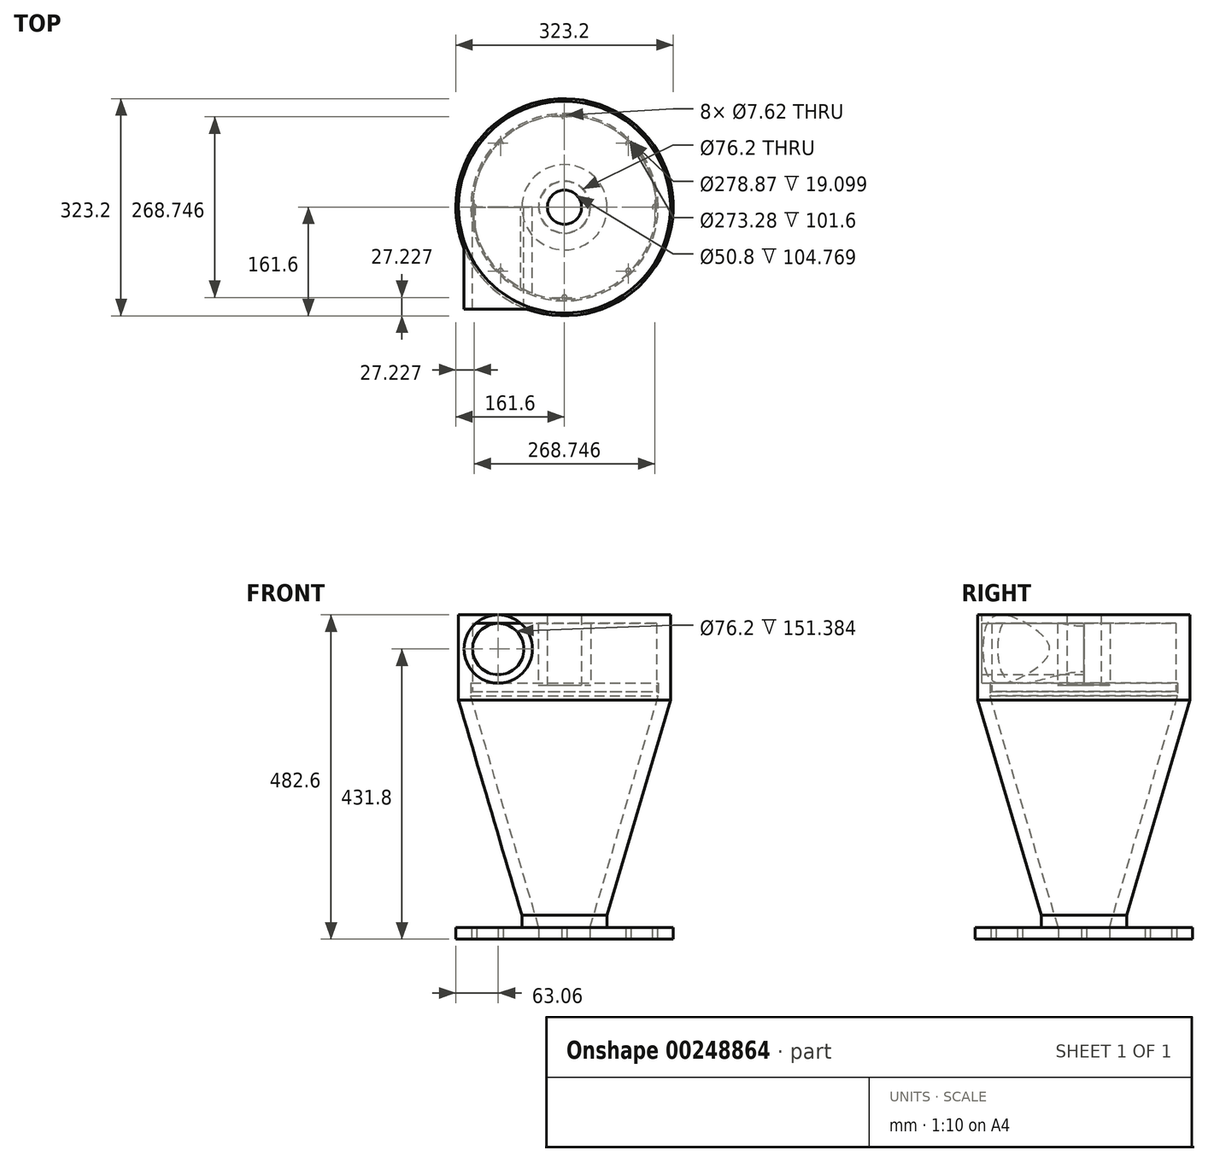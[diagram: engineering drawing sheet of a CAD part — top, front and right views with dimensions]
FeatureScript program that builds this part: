
annotation { "Feature Type Name" : "Feature", "Feature Type Description" : "" }
export const myFeature = defineFeature(function(context is Context, id is Id, definition is map)
    precondition{}
    {
        {
            var Q0;
            Q0=qCreatedBy(makeId("Front.planeOp"),FACE);
            var sketch = newSketch(context, id + "F0", { "sketchPlane" : qUnion([Q0])});
            skLineSegment(sketch, "E0.bottom", {"start": v(-38.1, 0) * mm, "end": v(-161.6, 0) * mm});
            skLineSegment(sketch, "E0.top", {"start": v(-63.5, 17.43) * mm, "end": v(-161.6, 17.43) * mm});
            skLineSegment(sketch, "E0.left", {"start": v(-38.1, 0) * mm, "end": v(-38.1, 17.43) * mm});
            skLineSegment(sketch, "E0.right", {"start": v(-161.6, 0) * mm, "end": v(-161.6, 17.43) * mm});
            skLineSegment(sketch, "E1", {"start": v(-38.1, 17.43) * mm, "end": v(-139.43, 361.9) * mm});
            skLineSegment(sketch, "E2", {"start": v(-157.57, 355.6) * mm, "end": v(-63.5, 35.82) * mm});
            skLineSegment(sketch, "E3", {"start": v(-63.5, 17.43) * mm, "end": v(-63.5, 35.82) * mm});
            skLineSegment(sketch, "E4", {"start": v(0, -75.28) * mm, "end": v(0, 555.19) * mm, "construction": true});
            skLineSegment(sketch, "E5.right", {"start": v(-139.43, 361.9) * mm, "end": v(-139.43, 361.9) * mm});
            skLineSegment(sketch, "E6.top", {"start": v(-139.43, 381) * mm, "end": v(-157.57, 381) * mm});
            skLineSegment(sketch, "E6.left", {"start": v(-139.43, 361.9) * mm, "end": v(-139.43, 381) * mm});
            skLineSegment(sketch, "E6.right", {"start": v(-157.57, 355.6) * mm, "end": v(-157.57, 381) * mm});
            skSolve(sketch);
        }
        {
            var Q0;
            Q0 = qSketchRegion(id + "F0", true);
            var Q1;
            Q1=sQuery(id+"F0.wireOp",EDGE,"E4");
            revolve(context, id + "F1", {"entities" : qUnion([Q0]), "axis" : qUnion([Q1]), "revolveType" : RevolveType.FULL});
        }
        {
            var Q0;
            Q0=makeQuery(id+"F1.opRevolve","SWEPT_FACE",FACE,{"disambiguationData":[OSD([sQuery(id+"F0.wireOp",EDGE,"E0.bottom")])]});
            var sketch = newSketch(context, id + "F2", { "sketchPlane" : qUnion([Q0])});
            skCircle(sketch, "E7", {"center": v(0, 134.37) * mm, "radius": 3.81 * mm});
            skLineSegment(sketch, "E8", {"start": v(0, 38.1) * mm, "end": v(0, 161.6) * mm, "construction": true});
            skCircle(sketch, "E9", {"center": v(0, 0) * mm, "radius": 134.37 * mm, "construction": true});
            skCircle(sketch, "E10.1.0", {"center": v(-95.02, 95.02) * mm, "radius": 3.81 * mm});
            skCircle(sketch, "E10.2.0", {"center": v(-134.37, 0) * mm, "radius": 3.81 * mm});
            skCircle(sketch, "E10.3.0", {"center": v(-95.02, -95.02) * mm, "radius": 3.81 * mm});
            skCircle(sketch, "E10.4.0", {"center": v(0, -134.37) * mm, "radius": 3.81 * mm});
            skCircle(sketch, "E10.5.0", {"center": v(95.02, -95.02) * mm, "radius": 3.81 * mm});
            skCircle(sketch, "E10.6.0", {"center": v(134.37, 0) * mm, "radius": 3.81 * mm});
            skCircle(sketch, "E10.7.0", {"center": v(95.02, 95.02) * mm, "radius": 3.81 * mm});
            skSolve(sketch);
        }
        {
            var Q0;
            Q0=makeQuery(id+"F2.imprint","IMPRINT",FACE,{"disambiguationData":[TD([[makeQuery(id+"F2.imprint","IMPRINT",EDGE,{"derivedFrom":sQuery(id+"F2.wireOp",EDGE,"E10.5.0")}),1.0]])]});
            var Q1;
            Q1=makeQuery(id+"F2.imprint","IMPRINT",FACE,{"disambiguationData":[TD([[makeQuery(id+"F2.imprint","IMPRINT",EDGE,{"derivedFrom":sQuery(id+"F2.wireOp",EDGE,"E10.4.0")}),1.0]])]});
            var Q2;
            Q2=makeQuery(id+"F2.imprint","IMPRINT",FACE,{"disambiguationData":[TD([[makeQuery(id+"F2.imprint","IMPRINT",EDGE,{"derivedFrom":sQuery(id+"F2.wireOp",EDGE,"E10.3.0")}),1.0]])]});
            var Q3;
            Q3=makeQuery(id+"F2.imprint","IMPRINT",FACE,{"disambiguationData":[TD([[makeQuery(id+"F2.imprint","IMPRINT",EDGE,{"derivedFrom":sQuery(id+"F2.wireOp",EDGE,"E10.2.0")}),1.0]])]});
            var Q4;
            Q4=makeQuery(id+"F2.imprint","IMPRINT",FACE,{"disambiguationData":[TD([[makeQuery(id+"F2.imprint","IMPRINT",EDGE,{"derivedFrom":sQuery(id+"F2.wireOp",EDGE,"E10.1.0")}),1.0]])]});
            var Q5;
            Q5=makeQuery(id+"F2.imprint","IMPRINT",FACE,{"disambiguationData":[TD([[makeQuery(id+"F2.imprint","IMPRINT",EDGE,{"derivedFrom":sQuery(id+"F2.wireOp",EDGE,"E7")}),1.0]])]});
            var Q6;
            Q6=makeQuery(id+"F2.imprint","IMPRINT",FACE,{"disambiguationData":[TD([[makeQuery(id+"F2.imprint","IMPRINT",EDGE,{"derivedFrom":sQuery(id+"F2.wireOp",EDGE,"E10.6.0")}),1.0]])]});
            var Q7;
            Q7=makeQuery(id+"F2.imprint","IMPRINT",FACE,{"disambiguationData":[TD([[makeQuery(id+"F2.imprint","IMPRINT",EDGE,{"derivedFrom":sQuery(id+"F2.wireOp",EDGE,"E10.7.0")}),1.0]])]});
            var Q8;
            Q8=sQuery(id+"F2.wireOp",EDGE,"E10.1.0");
            var Q9;
            Q9=sQuery(id+"F2.wireOp",EDGE,"E7");
            var Q10;
            Q10=sQuery(id+"F2.wireOp",EDGE,"E10.7.0");
            var Q11;
            Q11=sQuery(id+"F2.wireOp",EDGE,"E10.6.0");
            var Q12;
            Q12=sQuery(id+"F2.wireOp",EDGE,"E10.5.0");
            var Q13;
            Q13=sQuery(id+"F2.wireOp",EDGE,"E10.4.0");
            var Q14;
            Q14=sQuery(id+"F2.wireOp",EDGE,"E10.3.0");
            var Q15;
            Q15=sQuery(id+"F2.wireOp",EDGE,"E10.2.0");
            extrude(context, id + "F3", {"entities" : qUnion([Q0, Q1, Q2, Q3, Q4, Q5, Q6, Q7]), "operationType" : NewBodyOperationType.REMOVE, "surfaceEntities" : qUnion([Q8, Q9, Q10, Q11, Q12, Q13, Q14, Q15]), "endBound" : BoundingType.UP_TO_NEXT, "oppositeDirection" : true, "depth" : 25.4 * mm});
        }
        {
            var Q0;
            Q0=qCreatedBy(makeId("Front.planeOp"),FACE);
            var sketch = newSketch(context, id + "F4", { "sketchPlane" : qUnion([Q0])});
            skLineSegment(sketch, "E11", {"start": v(-139.18, 368.3) * mm, "end": v(-139.43, 368.3) * mm, "construction": true});
            skLineSegment(sketch, "E12.bottom", {"start": v(-139.18, 368.3) * mm, "end": v(-136.64, 368.3) * mm});
            skLineSegment(sketch, "E12.left", {"start": v(-139.18, 368.3) * mm, "end": v(-139.18, 381) * mm});
            skLineSegment(sketch, "E12.right", {"start": v(-136.64, 368.3) * mm, "end": v(-136.64, 469.9) * mm});
            skLineSegment(sketch, "E13.top", {"start": v(-139.18, 381) * mm, "end": v(-157.57, 381) * mm});
            skLineSegment(sketch, "E13.right", {"start": v(-157.57, 469.9) * mm, "end": v(-157.57, 381) * mm});
            skLineSegment(sketch, "E14.bottom", {"start": v(-136.64, 469.9) * mm, "end": v(-38.8, 469.9) * mm});
            skLineSegment(sketch, "E14.top", {"start": v(-157.57, 482.6) * mm, "end": v(-25.4, 482.6) * mm});
            skLineSegment(sketch, "E14.left", {"start": v(-157.57, 469.9) * mm, "end": v(-157.57, 482.6) * mm});
            skLineSegment(sketch, "E15.bottom", {"start": v(-25.4, 482.6) * mm, "end": v(-38.8, 482.6) * mm});
            skLineSegment(sketch, "E15.top", {"start": v(-25.4, 377.83) * mm, "end": v(-38.8, 377.83) * mm});
            skLineSegment(sketch, "E15.left", {"start": v(-25.4, 482.6) * mm, "end": v(-25.4, 377.83) * mm});
            skLineSegment(sketch, "E15.right", {"start": v(-38.8, 469.9) * mm, "end": v(-38.8, 377.83) * mm});
            skPoint(sketch, "E14.right.end.orphan", {"position": v(0, 482.6) * mm});
            skCircle(sketch, "E16", {"center": v(-98.54, 431.8) * mm, "radius": 38.1 * mm, "construction": true});
            skPoint(sketch, "E16.first.point", {"position": v(-136.64, 431.8) * mm});
            skPoint(sketch, "E16.second.point", {"position": v(-87.72, 468.33) * mm});
            skPoint(sketch, "E16.second.point.positionSnap0", {"position": v(-87.72, 469.9) * mm});
            skPoint(sketch, "E16.third.point", {"position": v(-60.47, 430.37) * mm});
            skSolve(sketch);
        }
        {
            var Q0;
            Q0 = qSketchRegion(id + "F4", true);
            var Q1;
            Q1=sQuery(id+"F0.wireOp",EDGE,"E4");
            revolve(context, id + "F5", {"entities" : qUnion([Q0]), "axis" : qUnion([Q1]), "revolveType" : RevolveType.FULL});
        }
        {
            var Q0;
            Q0=qCreatedBy(makeId("Front.planeOp"),FACE);
            var sketch = newSketch(context, id + "F6", { "sketchPlane" : qUnion([Q0])});
            skCircle(sketch, "E17", {"center": v(-98.54, 431.8) * mm, "radius": 50.8 * mm});
            skCircle(sketch, "E18", {"center": v(-98.54, 431.8) * mm, "radius": 38.1 * mm});
            skSolve(sketch);
        }
        {
            var Q0;
            Q0 = qSketchRegion(id + "F6", true);
            extrude(context, id + "F7", {"entities" : qUnion([Q0]), "operationType" : NewBodyOperationType.ADD, "depth" : 151.38 * mm});
        }
        {
            var Q0;
            Q0=qCreatedBy(makeId("Front.planeOp"),FACE);
            var sketch = newSketch(context, id + "F8", { "sketchPlane" : qUnion([Q0])});
            skCircle(sketch, "E19", {"center": v(-98.54, 431.8) * mm, "radius": 38.1 * mm});
            skSolve(sketch);
        }
        {
            var Q0;
            Q0 = qSketchRegion(id + "F8", true);
            extrude(context, id + "F9", {"entities" : qUnion([Q0]), "operationType" : NewBodyOperationType.REMOVE, "depth" : 150.88 * mm});
        }
    });
